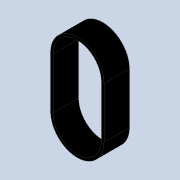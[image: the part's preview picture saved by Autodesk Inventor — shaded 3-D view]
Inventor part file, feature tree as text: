
AUTODESK INVENTOR PART (.ipt)
format: ipt  version: 2020 (Build 240168000, 168)  size: 98,816 bytes
history: native  units: mm
features: extrude x1, sketch x1
ambient origin geometry x8: Origin, YZ Plane, XZ Plane, XY Plane, X Axis, Y Axis, Z Axis, Center Point
bodies: Solid1 (feature_tree)
feature tree (2):
  extrude  "Extrusion1"  Depth=16.0mm
  sketch  "Sketch1"  dims[d3=9.5mm d4=16.0mm d5=1.0mm d6=10.0mm d7=0.0mm]
